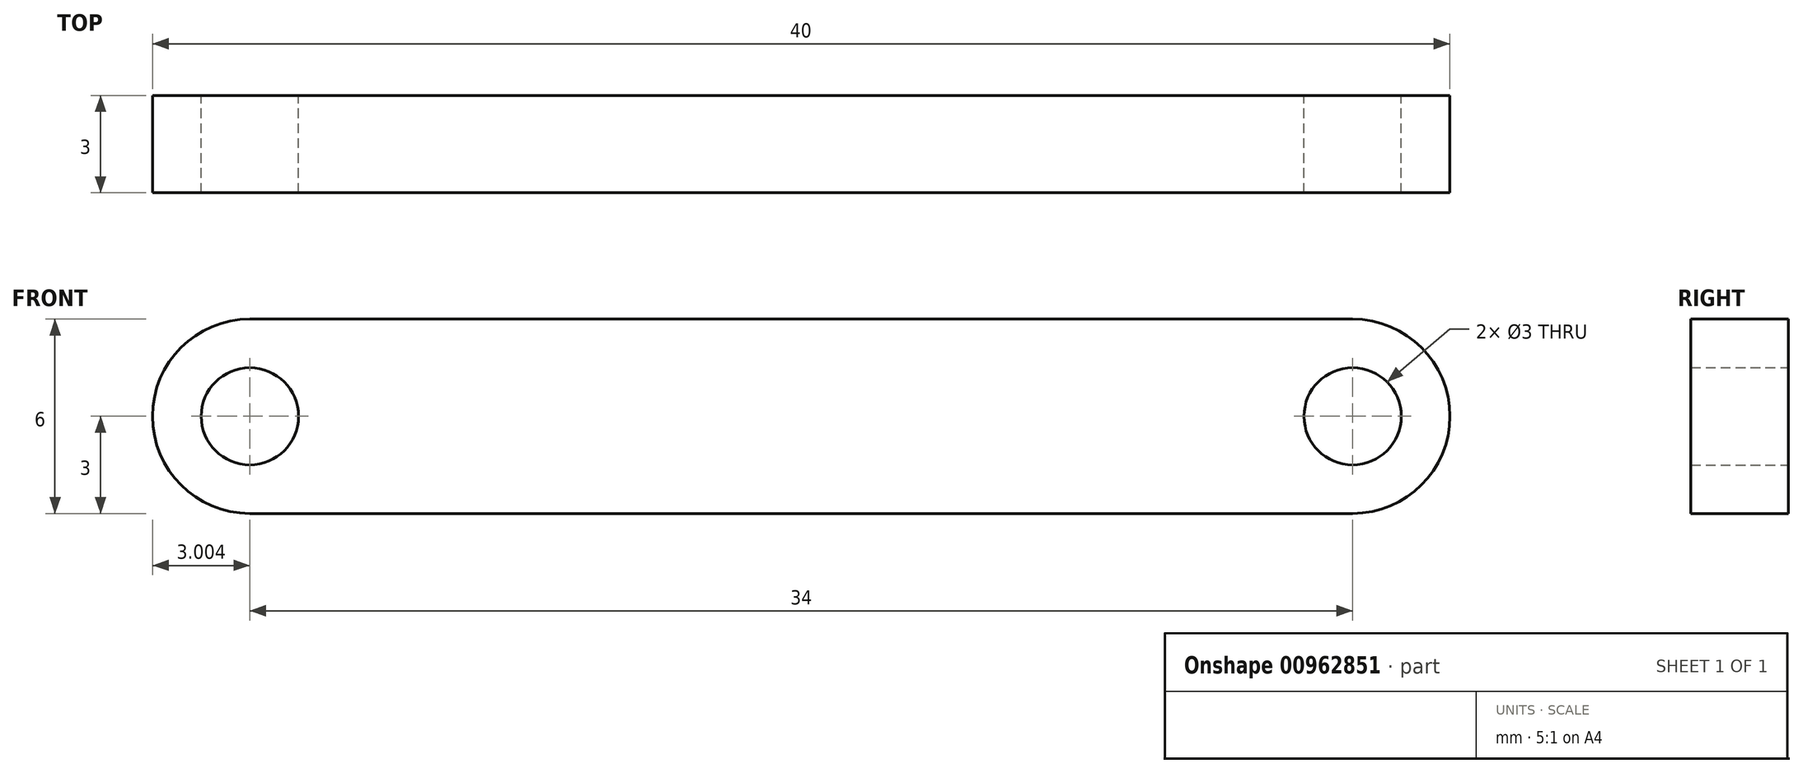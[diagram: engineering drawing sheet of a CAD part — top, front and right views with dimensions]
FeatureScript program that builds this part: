
annotation { "Feature Type Name" : "Feature", "Feature Type Description" : "" }
export const myFeature = defineFeature(function(context is Context, id is Id, definition is map)
    precondition{}
    {
        {
            var Q0;
            Q0=qCreatedBy(makeId("Front.planeOp"),FACE);
            var sketch = newSketch(context, id + "F0", { "sketchPlane" : qUnion([Q0])});
            skLineSegment(sketch, "E0.bottom", {"start": v(-30, 15) * mm, "end": v(0, 15) * mm});
            skLineSegment(sketch, "E0.top", {"start": v(-30, 0) * mm, "end": v(0, 0) * mm});
            skLineSegment(sketch, "E0.left", {"start": v(-30, 15) * mm, "end": v(-30, 0) * mm});
            skLineSegment(sketch, "E0.right", {"start": v(0, 15) * mm, "end": v(0, 0) * mm});
            skLineSegment(sketch, "E1.bottom", {"start": v(-50.6, 6) * mm, "end": v(-84.6, 6) * mm});
            skLineSegment(sketch, "E1.top", {"start": v(-50.6, 0) * mm, "end": v(-84.6, 0) * mm});
            skLineSegment(sketch, "E1.left", {"start": v(-47.6, 3) * mm, "end": v(-47.6, 3) * mm});
            skLineSegment(sketch, "E1.right", {"start": v(-87.6, 3) * mm, "end": v(-87.6, 3) * mm});
            skPoint(sketch, "E2.visualSharp", {"position": v(-87.6, 6) * mm});
            skArc(sketch, "E2.filletArc", {"start": v(-84.6, 6) * mm, "mid": v(-86.73, 5.12) * mm, "end": v(-87.6, 3) * mm});
            skPoint(sketch, "E3.visualSharp", {"position": v(-87.6, 0) * mm});
            skArc(sketch, "E3.filletArc", {"start": v(-87.6, 3) * mm, "mid": v(-86.73, 0.88) * mm, "end": v(-84.6, 0) * mm});
            skPoint(sketch, "E4.visualSharp", {"position": v(-47.6, 0) * mm});
            skArc(sketch, "E4.filletArc", {"start": v(-50.6, 0) * mm, "mid": v(-48.48, 0.88) * mm, "end": v(-47.6, 3) * mm});
            skPoint(sketch, "E5.visualSharp", {"position": v(-47.6, 6) * mm});
            skArc(sketch, "E5.filletArc", {"start": v(-47.6, 3) * mm, "mid": v(-48.48, 5.12) * mm, "end": v(-50.6, 6) * mm});
            skCircle(sketch, "E6", {"center": v(-84.6, 3) * mm, "radius": 1.5 * mm});
            skCircle(sketch, "E7", {"center": v(-50.6, 3) * mm, "radius": 1.5 * mm});
            skLineSegment(sketch, "E8.bottom", {"start": v(-30, 0) * mm, "end": v(-33, 0) * mm});
            skLineSegment(sketch, "E8.top", {"start": v(-30, 6) * mm, "end": v(-33, 6) * mm});
            skLineSegment(sketch, "E8.left", {"start": v(-30, 0) * mm, "end": v(-30, 6) * mm});
            skLineSegment(sketch, "E8.right", {"start": v(-36, 3) * mm, "end": v(-36, 3) * mm});
            skPoint(sketch, "E9.visualSharp", {"position": v(-36, 6) * mm});
            skArc(sketch, "E9.filletArc", {"start": v(-33, 6) * mm, "mid": v(-35.12, 5.12) * mm, "end": v(-36, 3) * mm});
            skPoint(sketch, "E10.visualSharp", {"position": v(-36, 0) * mm});
            skArc(sketch, "E10.filletArc", {"start": v(-36, 3) * mm, "mid": v(-35.12, 0.88) * mm, "end": v(-33, 0) * mm});
            skCircle(sketch, "E11", {"center": v(-33, 3) * mm, "radius": 1.5 * mm});
            skSolve(sketch);
        }
        {
            var Q0;
            Q0=makeQuery(id+"F0.imprint","IMPRINT",FACE,{"disambiguationData":[TD([[makeQuery(id+"F0.imprint","IMPRINT",EDGE,{"derivedFrom":sQuery(id+"F0.wireOp",EDGE,"E1.bottom")}),1.0]])]});
            extrude(context, id + "F1", {"entities" : qUnion([Q0]), "depth" : 3 * mm, "offsetDistance" : 25 * mm});
        }
    });
